# Revit family: Nivellierbare Kassette mit Schnurauslass, RKSRNUZD3, 20-25, 4
name_source: partatom
category: Generic Models
revit_build: Autodesk Revit 2015 (Build: 20140606_1530(x64)
units: mm (PartAtom-declared; Revit-internal decimal feet)

## types (4) — shared parameters
Diameter = 214 mm  [stored 0.7021 ft]
Height = 94 mm  [stored 0.308399 ft]
Height 1 = 37 mm
Manufacturer = OBO Bettermann
URL = http://www.obo-bettermann.com

## per-type parameters (varying)
| type | Cut depth | GTIN | Manufacturer Art.No. | Material |
| RKSRN2UZD3R4VS20 | 20 mm  [stored 0.0656168 ft] | 4012195867678 | 7409288 | Stainless Steel, Polished |
| RKSRN2UZD3R4VS25 | 25 mm  [stored 0.082021 ft] | 4012195867685 | 7409290 | Stainless Steel |
| RKSRN2UZD3R4MS20 | 20 mm  [stored 0.0656168 ft] | 4012195867630 | 7409282 | Brass, Soft Yellow, Welded |
| RKSRN2UZD3R4MS25 | 25 mm  [stored 0.082021 ft] | 4012195867661 | 7409284 | Brass, Soft Yellow, Welded |

note: column(s) folded — value = type name in every type: Article Type

note: [stored X ft] marks values corroborated as IEEE doubles in the binary element streams (Revit-internal decimal feet)

## geometry (parser evidence)
native form markers: Sweep x2
no freeform markers — native parametric forms only
